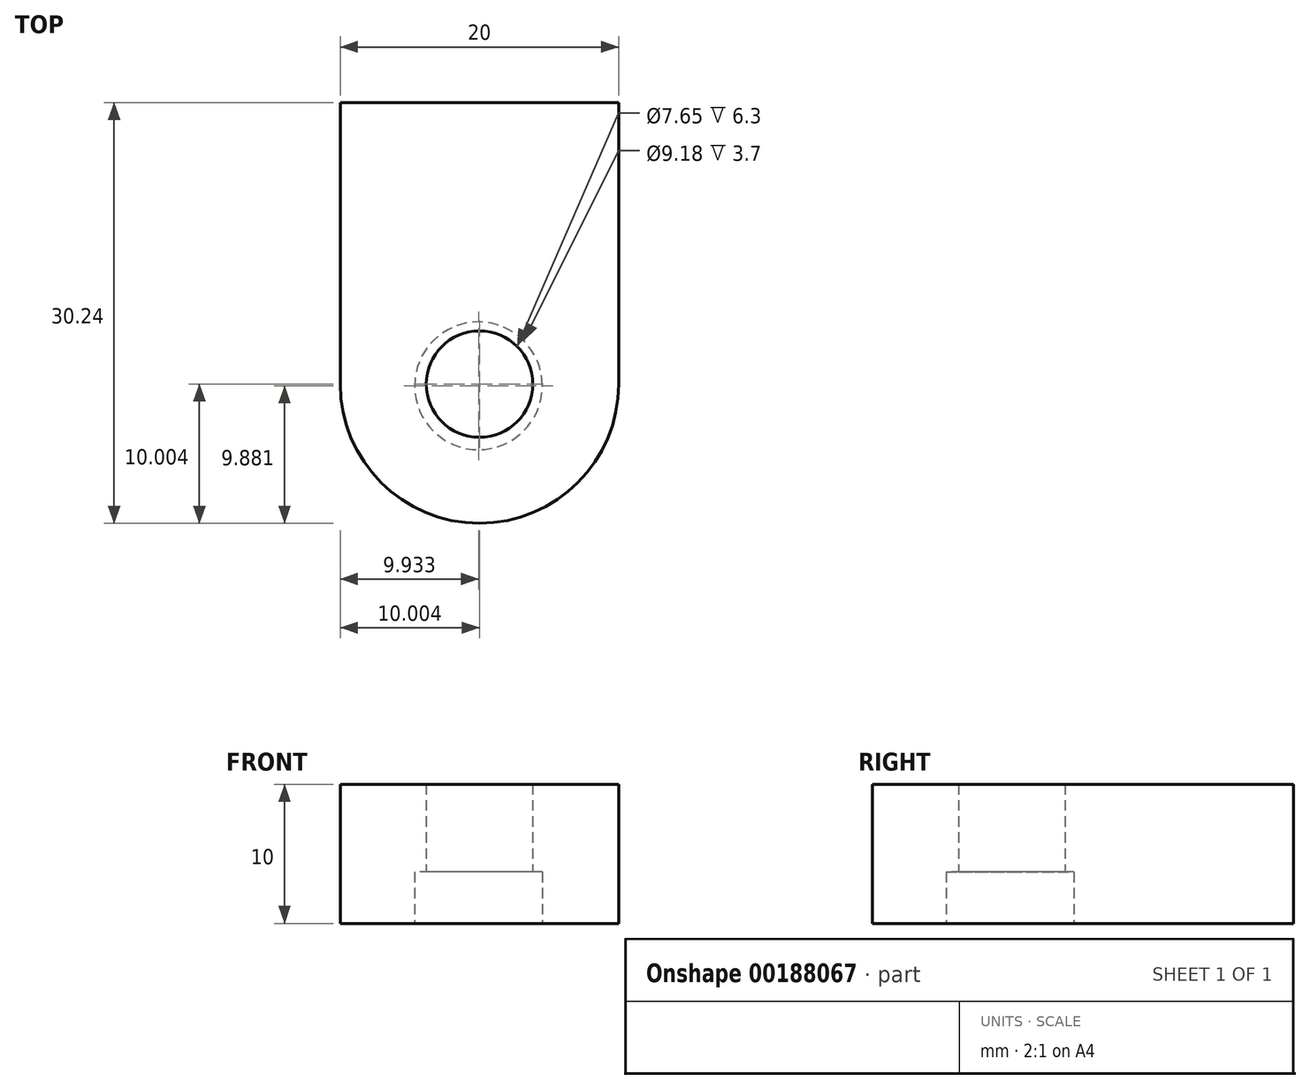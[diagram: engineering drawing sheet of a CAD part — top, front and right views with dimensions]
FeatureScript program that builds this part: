
annotation { "Feature Type Name" : "Feature", "Feature Type Description" : "" }
export const myFeature = defineFeature(function(context is Context, id is Id, definition is map)
    precondition{}
    {
        {
            var Q0;
            Q0=qCreatedBy(makeId("Top.planeOp"),FACE);
            var sketch = newSketch(context, id + "F0", { "sketchPlane" : qUnion([Q0])});
            skLineSegment(sketch, "E0", {"start": v(13.46, 43.26) * mm, "end": v(33.46, 43.26) * mm});
            skLineSegment(sketch, "E1", {"start": v(13.46, 43.26) * mm, "end": v(13.46, 27.72) * mm});
            skLineSegment(sketch, "E2", {"start": v(13.46, 27.72) * mm, "end": v(13.46, 23.02) * mm});
            skLineSegment(sketch, "E3", {"start": v(33.46, 43.26) * mm, "end": v(33.46, 23.02) * mm});
            skArc(sketch, "E4", {"start": v(13.46, 23.02) * mm, "mid": v(23.46, 13.02) * mm, "end": v(33.46, 23.02) * mm});
            skCircle(sketch, "E5", {"center": v(23.46, 23.02) * mm, "radius": 6.19 * mm});
            skCircle(sketch, "E6", {"center": v(23.46, 23.02) * mm, "radius": 3.82 * mm});
            skSolve(sketch);
        }
        {
            var Q0;
            Q0=qCreatedBy(makeId("Top.planeOp"),FACE);
            var sketch = newSketch(context, id + "F1", { "sketchPlane" : qUnion([Q0])});
            skSolve(sketch);
        }
        {
            var Q0;
            Q0 = qSketchRegion(id + "F1", true);
            var Q1;
            Q1=makeQuery(id+"F0.imprint","IMPRINT",FACE,{"disambiguationData":[TD([[makeQuery(id+"F0.imprint","IMPRINT",EDGE,{"derivedFrom":sQuery(id+"F0.wireOp",EDGE,"E5")}),1.0]])]});
            var Q2;
            Q2=makeQuery(id+"F0.imprint","IMPRINT",FACE,{"disambiguationData":[TD([[makeQuery(id+"F0.imprint","IMPRINT",EDGE,{"derivedFrom":sQuery(id+"F0.wireOp",EDGE,"E0")}),-1.0]])]});
            extrude(context, id + "F2", {"entities" : qUnion([Q0, Q1, Q2]), "depth" : 10 * mm});
        }
        {
            var Q0;
            Q0=qCreatedBy(makeId("Top.planeOp"),FACE);
            var sketch = newSketch(context, id + "F3", { "sketchPlane" : qUnion([Q0])});
            skCircle(sketch, "E7", {"center": v(23.4, 22.9) * mm, "radius": 4.59 * mm});
            skSolve(sketch);
        }
        {
            var Q0;
            Q0 = qSketchRegion(id + "F3", true);
            extrude(context, id + "F4", {"entities" : qUnion([Q0]), "operationType" : NewBodyOperationType.REMOVE, "depth" : 3.7 * mm});
        }
    });
